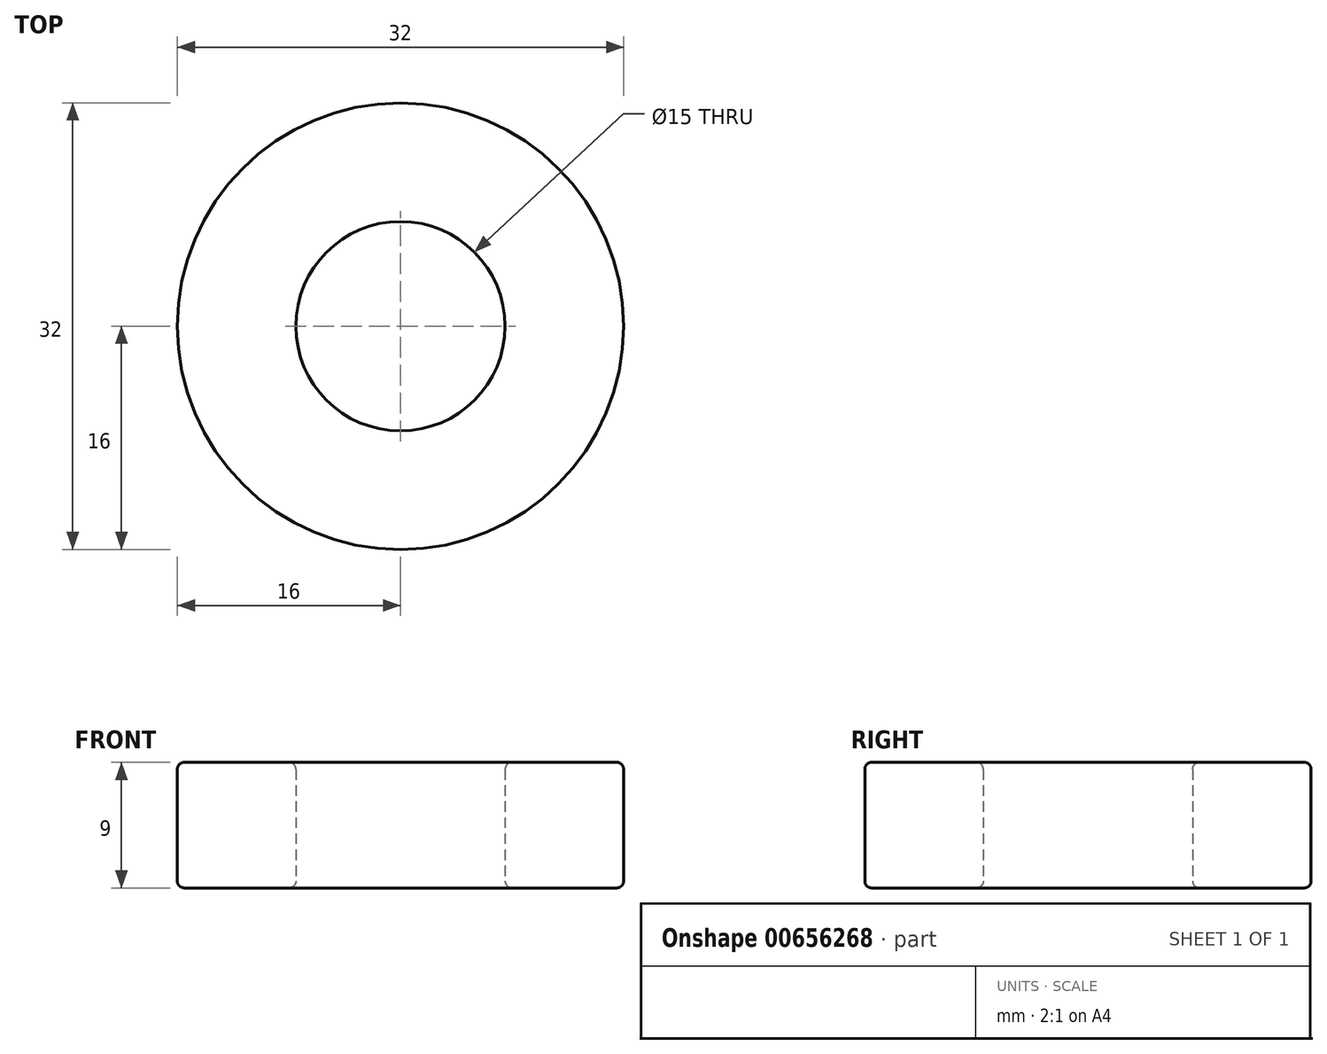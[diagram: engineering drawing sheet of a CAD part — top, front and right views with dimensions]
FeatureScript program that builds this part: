
annotation { "Feature Type Name" : "Feature", "Feature Type Description" : "" }
export const myFeature = defineFeature(function(context is Context, id is Id, definition is map)
    precondition{}
    {
        {
            var Q0;
            Q0=qCreatedBy(makeId("Top.planeOp"),FACE);
            var sketch = newSketch(context, id + "F0", { "sketchPlane" : qUnion([Q0])});
            skCircle(sketch, "E0", {"center": v(0, 0) * mm, "radius": 7.5 * mm});
            skCircle(sketch, "E1", {"center": v(0, 0) * mm, "radius": 16 * mm});
            skSolve(sketch);
        }
        {
            var Q0;
            Q0=makeQuery(id+"F0.imprint","IMPRINT",FACE,{"disambiguationData":[TD([[makeQuery(id+"F0.imprint","IMPRINT",EDGE,{"derivedFrom":sQuery(id+"F0.wireOp",EDGE,"E0")}),-1.0]])]});
            extrude(context, id + "F1", {"entities" : qUnion([Q0]), "depth" : 9 * mm, "offsetDistance" : 25 * mm});
        }
        {
            var Q0;
            Q0=makeQuery(id+"F1.opExtrude","CAP_FACE",FACE,{"disambiguationData":[OSD([sQuery(id+"F0.wireOp",EDGE,"E0"),sQuery(id+"F0.wireOp",EDGE,"E1")])],"isStart":false});
            var Q1;
            Q1=makeQuery(id+"F1.opExtrude","CAP_FACE",FACE,{"disambiguationData":[OSD([sQuery(id+"F0.wireOp",EDGE,"E0"),sQuery(id+"F0.wireOp",EDGE,"E1")])],"isStart":true});
            fillet(context, id + "F2", {"entities" : qUnion([Q0, Q1]), "radius" : 0.5 * mm, "tangentPropagation" : true, "allowEdgeOverflow" : false});
        }
    });
